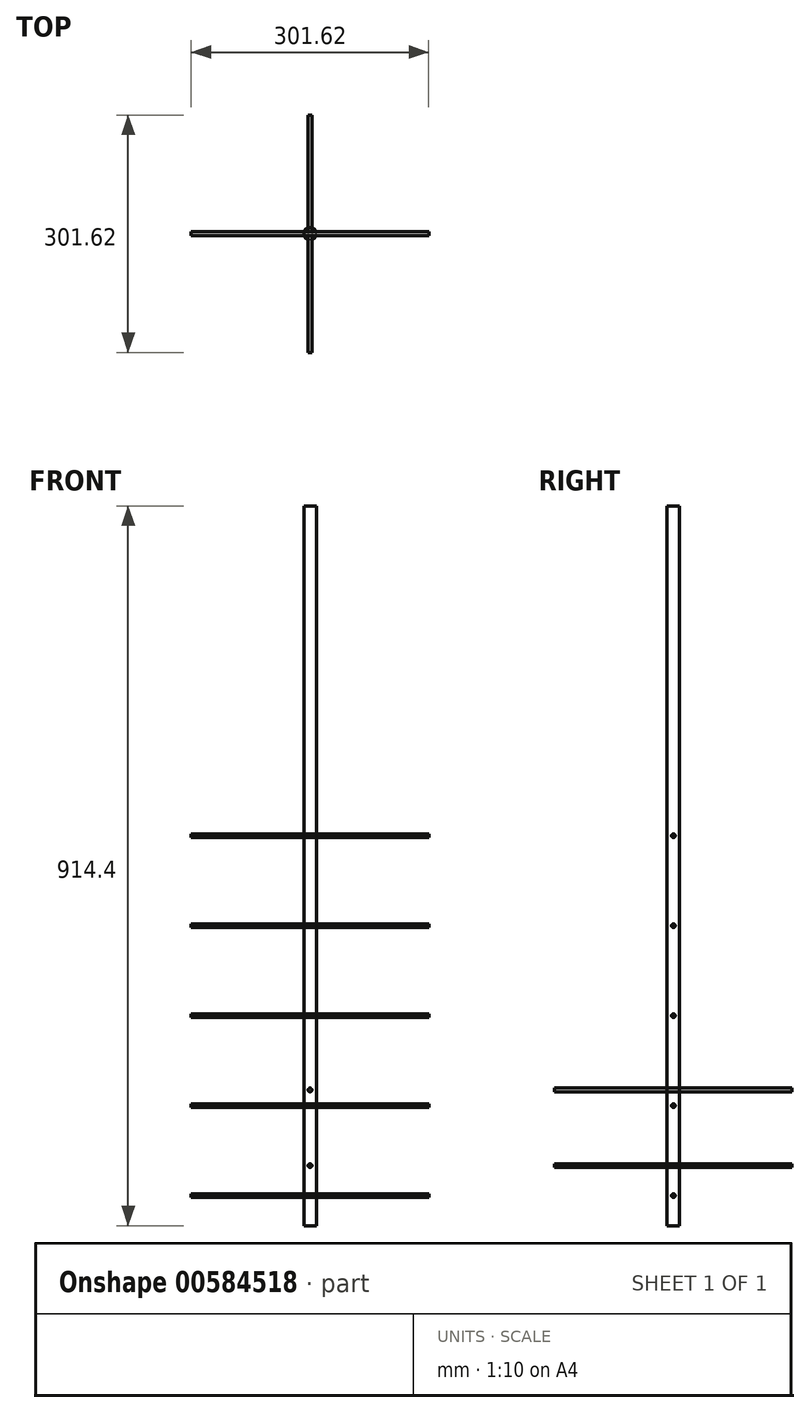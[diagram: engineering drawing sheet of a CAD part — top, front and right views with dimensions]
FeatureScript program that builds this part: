
annotation { "Feature Type Name" : "Feature", "Feature Type Description" : "" }
export const myFeature = defineFeature(function(context is Context, id is Id, definition is map)
    precondition{}
    {
        {
            var Q0;
            Q0=qCreatedBy(makeId("Top.planeOp"),FACE);
            var sketch = newSketch(context, id + "F0", { "sketchPlane" : qUnion([Q0])});
            skCircle(sketch, "E0", {"center": v(0, 0) * mm, "radius": 7.94 * mm});
            skSolve(sketch);
        }
        {
            var Q0;
            Q0=sQuery(id+"F0.wireOp",EDGE,"E0");
            extrude(context, id + "F1", {"bodyType" : ToolBodyType.SURFACE, "surfaceEntities" : qUnion([Q0]), "depth" : 914.4 * mm, "offsetDistance" : 25.4 * mm});
        }
        {
            var Q0;
            Q0=qCreatedBy(makeId("Right.planeOp"),FACE);
            var sketch = newSketch(context, id + "F2", { "sketchPlane" : qUnion([Q0])});
            skLineSegment(sketch, "E1", {"start": v(0, 0) * mm, "end": v(0, 38.1) * mm});
            skLineSegment(sketch, "E2", {"start": v(0, 38.1) * mm, "end": v(0, 76.2) * mm});
            skLineSegment(sketch, "E3", {"start": v(0, 76.2) * mm, "end": v(0, 114.3) * mm});
            skLineSegment(sketch, "E4", {"start": v(0, 114.3) * mm, "end": v(0, 152.4) * mm});
            skLineSegment(sketch, "E5", {"start": v(0, 152.4) * mm, "end": v(0, 190.5) * mm});
            skLineSegment(sketch, "E6", {"start": v(0, 190.5) * mm, "end": v(0, 228.6) * mm});
            skLineSegment(sketch, "E7", {"start": v(0, 228.6) * mm, "end": v(0, 266.7) * mm});
            skLineSegment(sketch, "E8", {"start": v(0, 266.7) * mm, "end": v(0, 304.8) * mm});
            skLineSegment(sketch, "E9", {"start": v(0, 304.8) * mm, "end": v(0, 342.9) * mm});
            skLineSegment(sketch, "E10", {"start": v(0, 342.9) * mm, "end": v(0, 381) * mm});
            skLineSegment(sketch, "E11", {"start": v(0, 381) * mm, "end": v(0, 419.1) * mm});
            skLineSegment(sketch, "E12", {"start": v(0, 419.1) * mm, "end": v(0, 457.2) * mm});
            skLineSegment(sketch, "E13", {"start": v(0, 457.2) * mm, "end": v(0, 495.3) * mm});
            skLineSegment(sketch, "E14", {"start": v(0, 495.3) * mm, "end": v(0, 533.4) * mm});
            skLineSegment(sketch, "E15", {"start": v(0, 533.4) * mm, "end": v(0, 571.5) * mm});
            skCircle(sketch, "E16", {"center": v(0, 38.1) * mm, "radius": 2.38 * mm});
            skCircle(sketch, "E17", {"center": v(0, 152.4) * mm, "radius": 2.38 * mm});
            skCircle(sketch, "E18", {"center": v(0, 266.7) * mm, "radius": 2.38 * mm});
            skCircle(sketch, "E19", {"center": v(0, 381) * mm, "radius": 2.38 * mm});
            skCircle(sketch, "E20", {"center": v(0, 495.3) * mm, "radius": 2.38 * mm});
            skSolve(sketch);
        }
        {
            var Q0;
            Q0=sQuery(id+"F2.wireOp",EDGE,"E16");
            extrude(context, id + "F3", {"bodyType" : ToolBodyType.SURFACE, "surfaceEntities" : qUnion([Q0]), "endBound" : BoundingType.SYMMETRIC, "depth" : 301.62 * mm, "offsetDistance" : 25.4 * mm});
        }
        {
            var Q0;
            Q0=sQuery(id+"F2.wireOp",EDGE,"E17");
            extrude(context, id + "F4", {"bodyType" : ToolBodyType.SURFACE, "surfaceEntities" : qUnion([Q0]), "endBound" : BoundingType.SYMMETRIC, "depth" : 301.62 * mm, "offsetDistance" : 25.4 * mm});
        }
        {
            var Q0;
            Q0=sQuery(id+"F2.wireOp",EDGE,"E18");
            extrude(context, id + "F5", {"bodyType" : ToolBodyType.SURFACE, "surfaceEntities" : qUnion([Q0]), "endBound" : BoundingType.SYMMETRIC, "depth" : 301.62 * mm, "offsetDistance" : 25.4 * mm});
        }
        {
            var Q0;
            Q0=sQuery(id+"F2.wireOp",EDGE,"E19");
            extrude(context, id + "F6", {"bodyType" : ToolBodyType.SURFACE, "surfaceEntities" : qUnion([Q0]), "endBound" : BoundingType.SYMMETRIC, "depth" : 301.62 * mm, "offsetDistance" : 25.4 * mm});
        }
        {
            var Q0;
            Q0=sQuery(id+"F2.wireOp",EDGE,"E20");
            extrude(context, id + "F7", {"bodyType" : ToolBodyType.SURFACE, "surfaceEntities" : qUnion([Q0]), "endBound" : BoundingType.SYMMETRIC, "depth" : 301.62 * mm, "offsetDistance" : 25.4 * mm});
        }
        {
            var Q0;
            Q0=qCreatedBy(makeId("Front.planeOp"),FACE);
            var sketch = newSketch(context, id + "F8", { "sketchPlane" : qUnion([Q0])});
            skLineSegment(sketch, "E21", {"start": v(0, 0) * mm, "end": v(0, 38.1) * mm});
            skLineSegment(sketch, "E22", {"start": v(0, 38.1) * mm, "end": v(0, 76.2) * mm});
            skLineSegment(sketch, "E23", {"start": v(0, 76.2) * mm, "end": v(0, 114.3) * mm});
            skLineSegment(sketch, "E24", {"start": v(0, 114.3) * mm, "end": v(0, 152.4) * mm});
            skCircle(sketch, "E25", {"center": v(0, 76.2) * mm, "radius": 2.38 * mm});
            skSolve(sketch);
        }
        {
            var Q0;
            Q0=sQuery(id+"F8.wireOp",EDGE,"E25");
            extrude(context, id + "F9", {"bodyType" : ToolBodyType.SURFACE, "surfaceEntities" : qUnion([Q0]), "endBound" : BoundingType.SYMMETRIC, "depth" : 301.62 * mm, "offsetDistance" : 25.4 * mm});
        }
        {
            var Q0;
            Q0=qCreatedBy(makeId("Front.planeOp"),FACE);
            var sketch = newSketch(context, id + "F10", { "sketchPlane" : qUnion([Q0])});
            skLineSegment(sketch, "E26", {"start": v(0, 77.13) * mm, "end": v(0, 115.23) * mm});
            skLineSegment(sketch, "E27", {"start": v(0, 115.23) * mm, "end": v(0, 153.33) * mm});
            skLineSegment(sketch, "E28", {"start": v(0, 153.33) * mm, "end": v(0, 191.43) * mm});
            skLineSegment(sketch, "E29", {"start": v(0, 191.43) * mm, "end": v(0, 229.53) * mm});
            skPoint(sketch, "E29.endSnap0", {"position": v(0, 172.38) * mm});
            skLineSegment(sketch, "E30", {"start": v(0, 229.53) * mm, "end": v(0, 267.63) * mm});
            skLineSegment(sketch, "E31", {"start": v(0, 267.63) * mm, "end": v(0, 305.73) * mm});
            skLineSegment(sketch, "E32", {"start": v(0, 305.73) * mm, "end": v(0, 343.83) * mm});
            skLineSegment(sketch, "E33", {"start": v(0, 343.83) * mm, "end": v(0, 381.93) * mm});
            skLineSegment(sketch, "E34", {"start": v(0, 381.93) * mm, "end": v(0, 420.03) * mm});
            skLineSegment(sketch, "E35", {"start": v(0, 420.03) * mm, "end": v(0, 458.13) * mm});
            skLineSegment(sketch, "E36", {"start": v(0, 458.13) * mm, "end": v(0, 496.23) * mm});
            skCircle(sketch, "E37", {"center": v(0, 172.38) * mm, "radius": 2.38 * mm});
            skCircle(sketch, "E38", {"center": v(0, 305.73) * mm, "radius": 2.38 * mm});
            skCircle(sketch, "E39", {"center": v(0, 420.03) * mm, "radius": 2.38 * mm});
            skSolve(sketch);
        }
        {
            var Q0;
            Q0=sQuery(id+"F10.wireOp",EDGE,"E37");
            extrude(context, id + "F11", {"bodyType" : ToolBodyType.SURFACE, "surfaceEntities" : qUnion([Q0]), "endBound" : BoundingType.SYMMETRIC, "depth" : 301.62 * mm, "offsetDistance" : 25.4 * mm});
        }
    });
